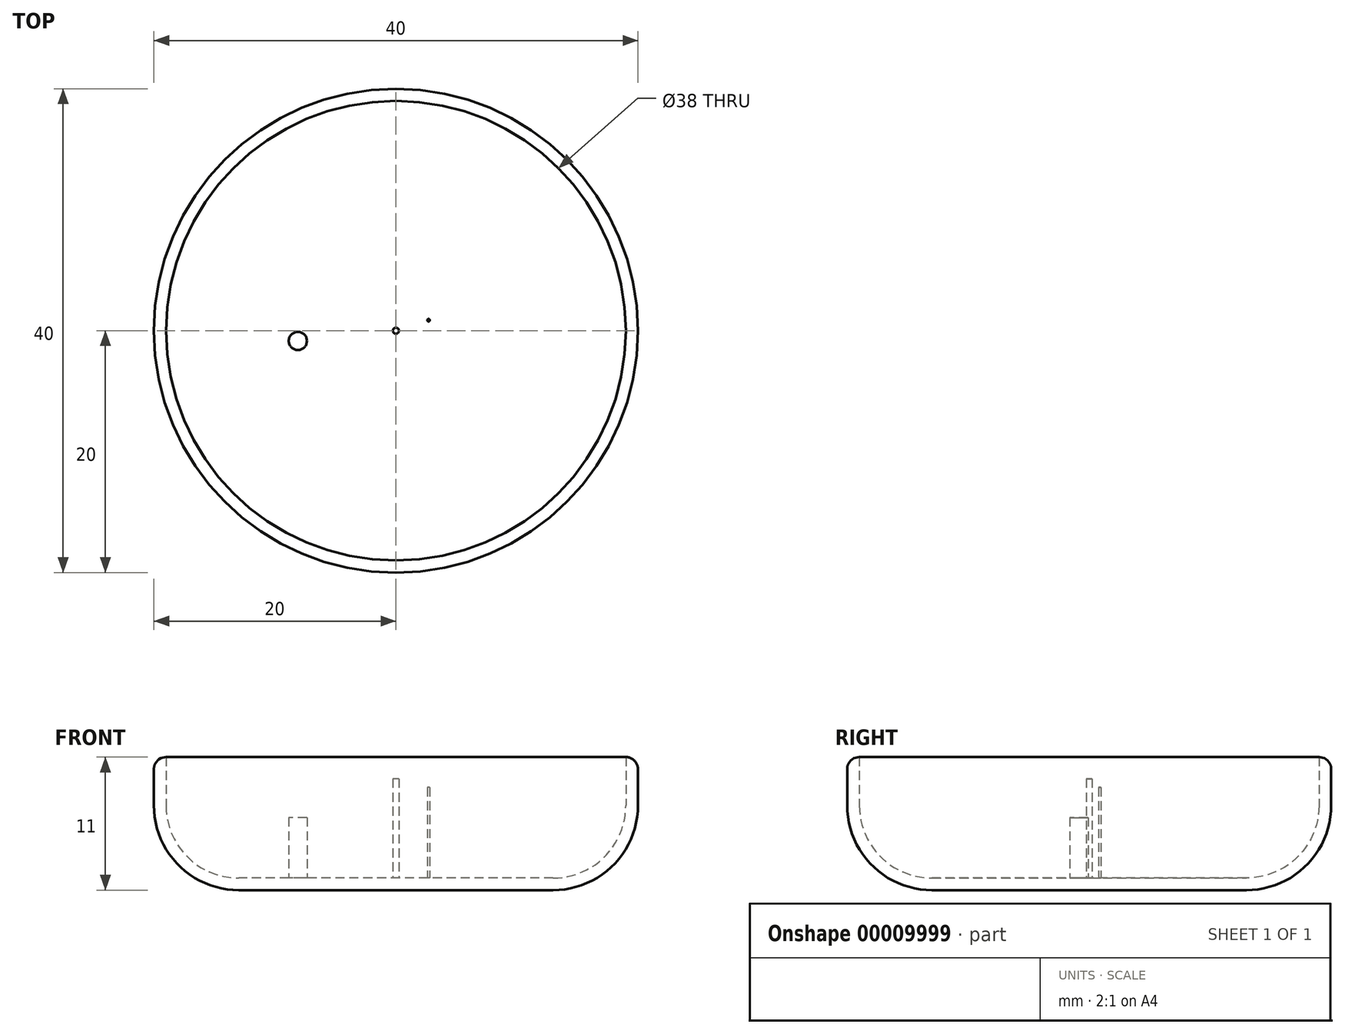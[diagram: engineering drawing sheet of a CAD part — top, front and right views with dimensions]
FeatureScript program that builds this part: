
annotation { "Feature Type Name" : "Feature", "Feature Type Description" : "" }
export const myFeature = defineFeature(function(context is Context, id is Id, definition is map)
    precondition{}
    {
        {
            var Q0;
            Q0=qCreatedBy(makeId("Top.planeOp"),FACE);
            var sketch = newSketch(context, id + "F0", { "sketchPlane" : qUnion([Q0])});
            skCircle(sketch, "E0", {"center": v(0, 0) * mm, "radius": 20 * mm});
            skSolve(sketch);
        }
        {
            var Q0;
            Q0=qSketchRegion(id+"F0",true);
            extrude(context, id + "F1", {"entities" : qUnion([Q0]), "depth" : 11 * mm});
        }
        {
            var Q0;
            Q0=makeQuery(id+"F1.opExtrude","CAP_EDGE",EDGE,{"disambiguationData":[OSD([sQuery(id+"F0.wireOp",EDGE,"E0")])],"isStart":true});
            fillet(context, id + "F2", {"entities" : qUnion([Q0]), "radius" : 7 * mm, "tangentPropagation" : true, "allowEdgeOverflow" : false});
        }
        {
            var Q0;
            Q0=makeQuery(id+"F1.opExtrude","CAP_FACE",FACE,{"disambiguationData":[OSD([sQuery(id+"F0.wireOp",EDGE,"E0")])],"isStart":false});
            shell(context, id + "F3", {"entities" : qUnion([Q0]), "thickness" : 1 * mm});
        }
        {
            var Q0;
            Q0=makeQuery(id+"F1.opExtrude","CAP_EDGE",EDGE,{"disambiguationData":[OSD([sQuery(id+"F0.wireOp",EDGE,"E0")])],"isStart":false});
            fillet(context, id + "F4", {"entities" : qUnion([Q0]), "radius" : 1 * mm, "tangentPropagation" : true, "allowEdgeOverflow" : false});
        }
        {
            var Q0;
            {var subQ0=sQuery(id+"F0.wireOp",EDGE,"E0");Q0=makeQuery(id+"F3.opShell","OFFSET_FACE",FACE,{"disambiguationData":[OSD([subQ0]),TDD([makeQuery(id+"F1.opExtrude","CAP_FACE",FACE,{"disambiguationData":[OSD([subQ0])],"isStart":true})])]});}
            var sketch = newSketch(context, id + "F5", { "sketchPlane" : qUnion([Q0])});
            skCircle(sketch, "E1", {"center": v(0, 0) * mm, "radius": 0.25 * mm});
            skCircle(sketch, "E2", {"center": v(-8.1, -0.84) * mm, "radius": 0.75 * mm});
            skCircle(sketch, "E3", {"center": v(2.7, 0.87) * mm, "radius": 0.1 * mm});
            skSolve(sketch);
        }
        {
            var Q0;
            Q0=qSketchRegion(id+"F5",true);
            extrude(context, id + "F6", {"entities" : qUnion([Q0]), "operationType" : NewBodyOperationType.ADD, "depth" : 10 * mm});
        }
        {
            var Q0;
            Q0=makeQuery(id+"F6.opExtrude","CAP_FACE",FACE,{"disambiguationData":[OSD([sQuery(id+"F5.wireOp",EDGE,"E2")])],"isStart":false});
            var sketch = newSketch(context, id + "F7", { "sketchPlane" : qUnion([Q0])});
            skCircle(sketch, "E4", {"center": v(-8.1, -0.84) * mm, "radius": 0.75 * mm});
            skSolve(sketch);
        }
        {
            var Q0;
            Q0 = qSketchRegion(id + "F7", true);
            extrude(context, id + "F8", {"entities" : qUnion([Q0]), "operationType" : NewBodyOperationType.REMOVE, "oppositeDirection" : true, "depth" : 5 * mm});
        }
        {
            var Q0;
            Q0=makeQuery(id+"F6.opExtrude","CAP_FACE",FACE,{"disambiguationData":[OSD([sQuery(id+"F5.wireOp",EDGE,"E3")])],"isStart":false});
            var sketch = newSketch(context, id + "F9", { "sketchPlane" : qUnion([Q0])});
            skCircle(sketch, "E5", {"center": v(2.7, 0.87) * mm, "radius": 0.1 * mm});
            skSolve(sketch);
        }
        {
            var Q0;
            Q0 = qSketchRegion(id + "F9", true);
            extrude(context, id + "F10", {"entities" : qUnion([Q0]), "operationType" : NewBodyOperationType.REMOVE, "oppositeDirection" : true, "depth" : 2.5 * mm});
        }
        {
            var Q0;
            Q0=makeQuery(id+"F6.opExtrude","CAP_FACE",FACE,{"disambiguationData":[OSD([sQuery(id+"F5.wireOp",EDGE,"E1")])],"isStart":false});
            var sketch = newSketch(context, id + "F11", { "sketchPlane" : qUnion([Q0])});
            skCircle(sketch, "E6", {"center": v(0, 0) * mm, "radius": 0.25 * mm});
            skSolve(sketch);
        }
        {
            var Q0;
            Q0 = qSketchRegion(id + "F11", true);
            extrude(context, id + "F12", {"entities" : qUnion([Q0]), "operationType" : NewBodyOperationType.REMOVE, "oppositeDirection" : true, "depth" : 1.8 * mm});
        }
    });
